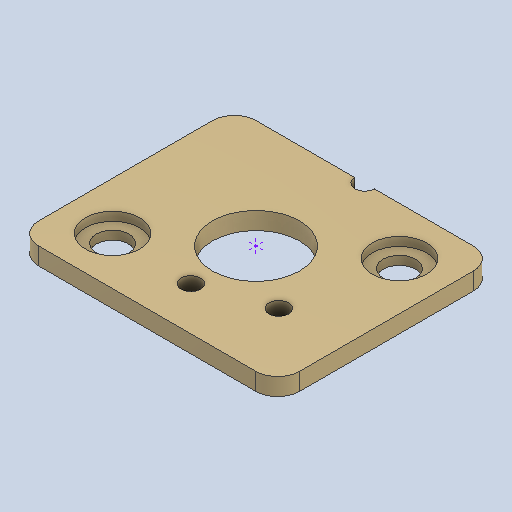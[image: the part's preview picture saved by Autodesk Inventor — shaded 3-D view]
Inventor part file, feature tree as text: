
AUTODESK INVENTOR PART (.ipt)
format: ipt  version: 2022 (Build 260153000, 153)  size: 126,464 bytes
history: native  units: mm
features: other x2, sketch x1
ambient origin geometry x8: Origin, YZ Plane, XZ Plane, XY Plane, X Axis, Y Axis, Z Axis, Center Point
bodies: Body1 (feature_tree)
feature tree (3):
  other  "Sólido1"
  sketch  "Esboço 3D1"
  other  "Sólido2"
